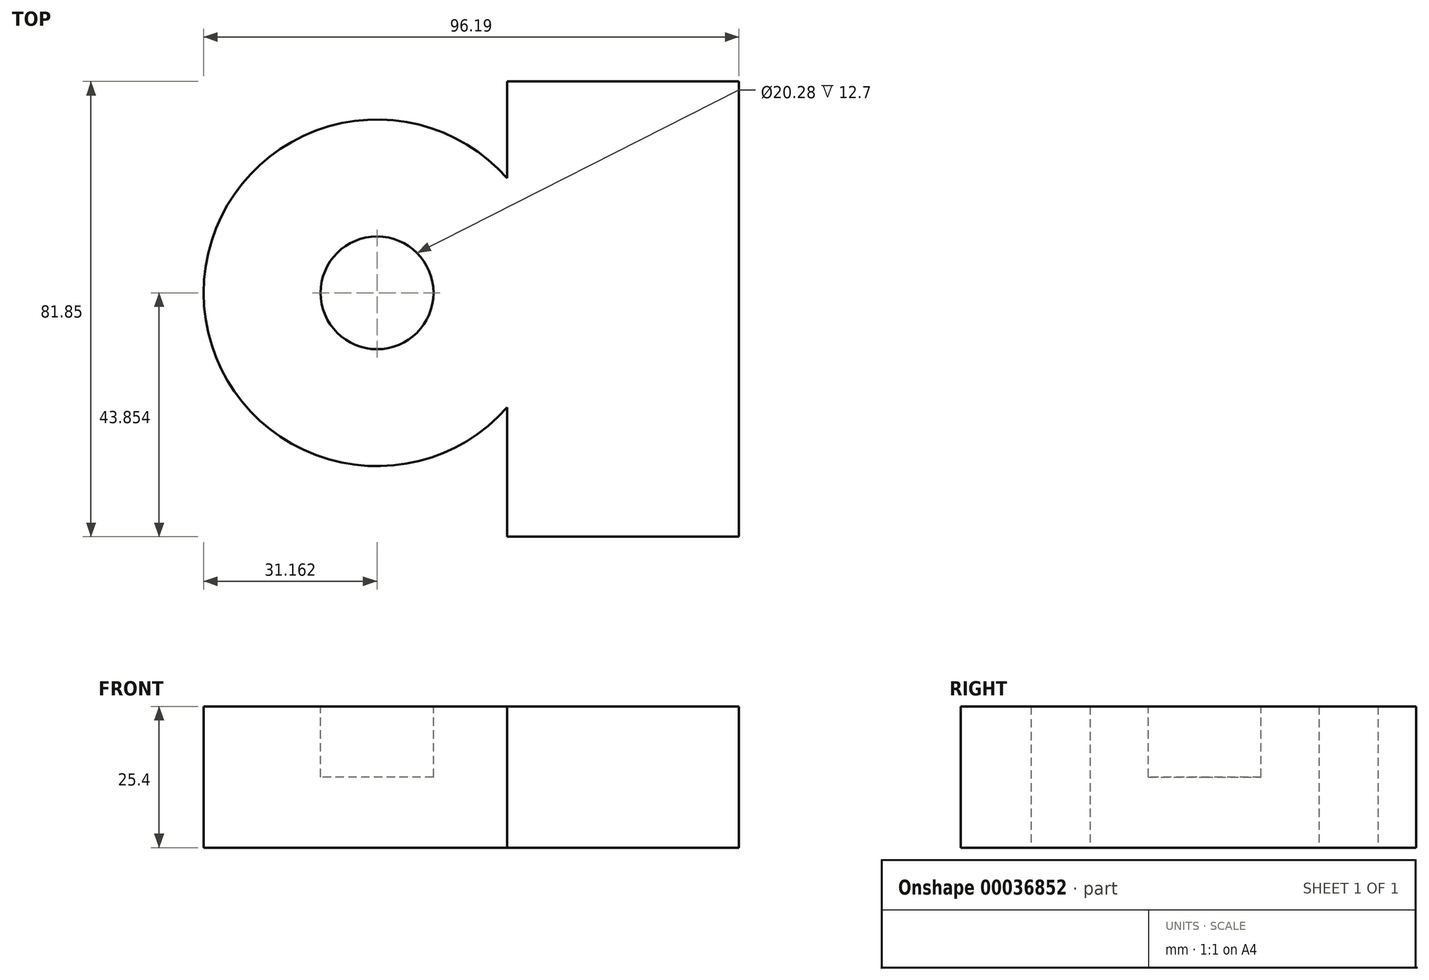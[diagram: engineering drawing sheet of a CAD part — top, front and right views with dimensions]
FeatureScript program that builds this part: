
annotation { "Feature Type Name" : "Feature", "Feature Type Description" : "" }
export const myFeature = defineFeature(function(context is Context, id is Id, definition is map)
    precondition{}
    {
        {
            var Q0;
            Q0=qCreatedBy(makeId("Top.planeOp"),FACE);
            var sketch = newSketch(context, id + "F0", { "sketchPlane" : qUnion([Q0])});
            skArc(sketch, "E0", {"start": v(-66.96, 13.75) * mm, "mid": v(-121.52, -6.84) * mm, "end": v(-66.96, -27.42) * mm});
            skLineSegment(sketch, "E1.bottom", {"start": v(-66.96, 31.16) * mm, "end": v(-25.33, 31.16) * mm});
            skLineSegment(sketch, "E1.top", {"start": v(-66.96, -50.7) * mm, "end": v(-25.33, -50.7) * mm});
            skLineSegment(sketch, "E1.left", {"start": v(-66.96, 31.16) * mm, "end": v(-66.96, 13.75) * mm});
            skLineSegment(sketch, "E1.right", {"start": v(-25.33, 31.16) * mm, "end": v(-25.33, -50.7) * mm});
            skLineSegment(sketch, "E2.trimOffspring", {"start": v(-66.96, -27.42) * mm, "end": v(-66.96, -50.7) * mm});
            skSolve(sketch);
        }
        {
            var Q0;
            Q0=makeQuery(id+"F0.imprint","IMPRINT",FACE,{"disambiguationData":[TD([[makeQuery(id+"F0.imprint","IMPRINT",EDGE,{"derivedFrom":sQuery(id+"F0.wireOp",EDGE,"E0")}),1.0]])]});
            extrude(context, id + "F1", {"entities" : qUnion([Q0]), "depth" : 25.4 * mm});
        }
        {
            var Q0;
            Q0=makeQuery(id+"F1.opExtrude","CAP_FACE",FACE,{"disambiguationData":[OSD([sQuery(id+"F0.wireOp",EDGE,"E0"),sQuery(id+"F0.wireOp",EDGE,"E1.bottom"),sQuery(id+"F0.wireOp",EDGE,"E1.top"),sQuery(id+"F0.wireOp",EDGE,"E1.left"),sQuery(id+"F0.wireOp",EDGE,"E1.right"),sQuery(id+"F0.wireOp",EDGE,"E2.trimOffspring")])],"isStart":false});
            var sketch = newSketch(context, id + "F2", { "sketchPlane" : qUnion([Q0])});
            skCircle(sketch, "E3", {"center": v(-90.36, -6.84) * mm, "radius": 10.14 * mm});
            skSolve(sketch);
        }
        {
            var Q0;
            Q0=makeQuery(id+"F2.imprint","IMPRINT",FACE,{"disambiguationData":[TD([[makeQuery(id+"F2.imprint","IMPRINT",EDGE,{"derivedFrom":sQuery(id+"F2.wireOp",EDGE,"E3")}),1.0]])]});
            extrude(context, id + "F3", {"entities" : qUnion([Q0]), "operationType" : NewBodyOperationType.REMOVE, "oppositeDirection" : true, "depth" : 12.7 * mm});
        }
    });
